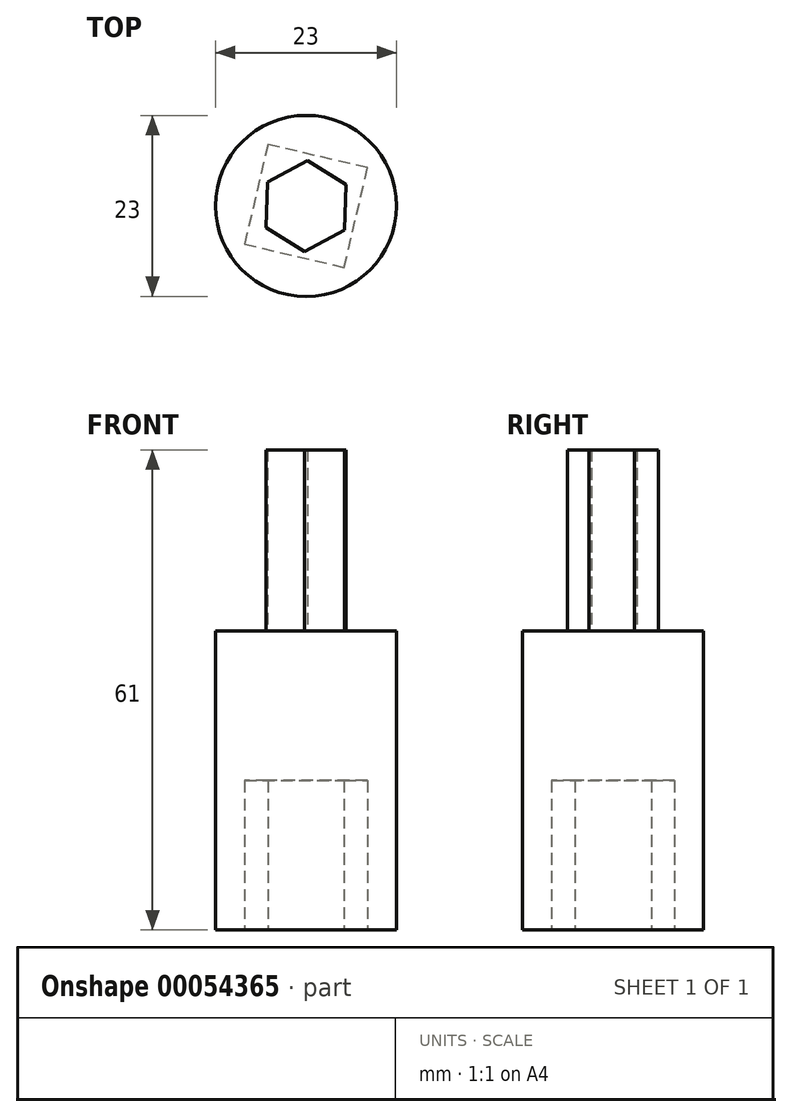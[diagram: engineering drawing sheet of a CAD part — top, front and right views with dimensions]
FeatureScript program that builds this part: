
annotation { "Feature Type Name" : "Feature", "Feature Type Description" : "" }
export const myFeature = defineFeature(function(context is Context, id is Id, definition is map)
    precondition{}
    {
        {
            var Q0;
            Q0=qCreatedBy(makeId("Top.planeOp"),FACE);
            var sketch = newSketch(context, id + "F0", { "sketchPlane" : qUnion([Q0])});
            skCircle(sketch, "E0", {"center": v(0, 0) * mm, "radius": 11.5 * mm});
            skSolve(sketch);
        }
        {
            var Q0;
            Q0=makeQuery(id+"F0.imprint","IMPRINT",FACE,{"disambiguationData":[TD([[makeQuery(id+"F0.imprint","IMPRINT",EDGE,{"derivedFrom":sQuery(id+"F0.wireOp",EDGE,"E0")}),1.0]])]});
            extrude(context, id + "F1", {"entities" : qUnion([Q0]), "depth" : 38 * mm});
        }
        {
            var Q0;
            Q0=makeQuery(id+"F1.opExtrude","CAP_FACE",FACE,{"disambiguationData":[OSD([sQuery(id+"F0.wireOp",EDGE,"E0")])],"isStart":false});
            var sketch = newSketch(context, id + "F2", { "sketchPlane" : qUnion([Q0])});
            skCircle(sketch, "E1.cCircle", {"center": v(0, 0) * mm, "radius": 5 * mm, "construction": true});
            skLineSegment(sketch, "E1.0", {"start": v(0.18, 5.77) * mm, "end": v(5.09, 2.73) * mm});
            skLineSegment(sketch, "E1.1", {"start": v(5.09, 2.73) * mm, "end": v(4.9, -3.04) * mm});
            skLineSegment(sketch, "E1.2", {"start": v(4.9, -3.04) * mm, "end": v(-0.18, -5.77) * mm});
            skLineSegment(sketch, "E1.3", {"start": v(-0.18, -5.77) * mm, "end": v(-5.09, -2.73) * mm});
            skLineSegment(sketch, "E1.4", {"start": v(-5.09, -2.73) * mm, "end": v(-4.9, 3.04) * mm});
            skLineSegment(sketch, "E1.5", {"start": v(-4.9, 3.04) * mm, "end": v(0.18, 5.77) * mm});
            skPoint(sketch, "E1.0.midPoint", {"position": v(2.63, 4.25) * mm});
            skSolve(sketch);
        }
        {
            var Q0;
            Q0=makeQuery(id+"F2.imprint","IMPRINT",FACE,{"disambiguationData":[TD([[makeQuery(id+"F2.imprint","IMPRINT",EDGE,{"derivedFrom":sQuery(id+"F2.wireOp",EDGE,"E1.0")}),-1.0]])]});
            extrude(context, id + "F3", {"entities" : qUnion([Q0]), "operationType" : NewBodyOperationType.ADD, "depth" : 23 * mm});
        }
        {
            var Q0;
            Q0=makeQuery(id+"F1.opExtrude","CAP_FACE",FACE,{"disambiguationData":[OSD([sQuery(id+"F0.wireOp",EDGE,"E0")])],"isStart":true});
            var sketch = newSketch(context, id + "F4", { "sketchPlane" : qUnion([Q0])});
            skCircle(sketch, "E2.cCircle", {"center": v(0, 0) * mm, "radius": 6.5 * mm, "construction": true});
            skLineSegment(sketch, "E2.0", {"start": v(4.85, 7.8) * mm, "end": v(7.8, -4.85) * mm});
            skLineSegment(sketch, "E2.1", {"start": v(7.8, -4.85) * mm, "end": v(-4.85, -7.8) * mm});
            skLineSegment(sketch, "E2.2", {"start": v(-4.85, -7.8) * mm, "end": v(-7.8, 4.85) * mm});
            skLineSegment(sketch, "E2.3", {"start": v(-7.8, 4.85) * mm, "end": v(4.85, 7.8) * mm});
            skPoint(sketch, "E2.0.midPoint", {"position": v(6.33, 1.48) * mm});
            skSolve(sketch);
        }
        {
            var Q0;
            Q0=makeQuery(id+"F4.imprint","IMPRINT",FACE,{"disambiguationData":[TD([[makeQuery(id+"F4.imprint","IMPRINT",EDGE,{"derivedFrom":sQuery(id+"F4.wireOp",EDGE,"E2.0")}),-1.0]])]});
            extrude(context, id + "F5", {"entities" : qUnion([Q0]), "operationType" : NewBodyOperationType.REMOVE, "oppositeDirection" : true, "depth" : 19 * mm});
        }
    });
